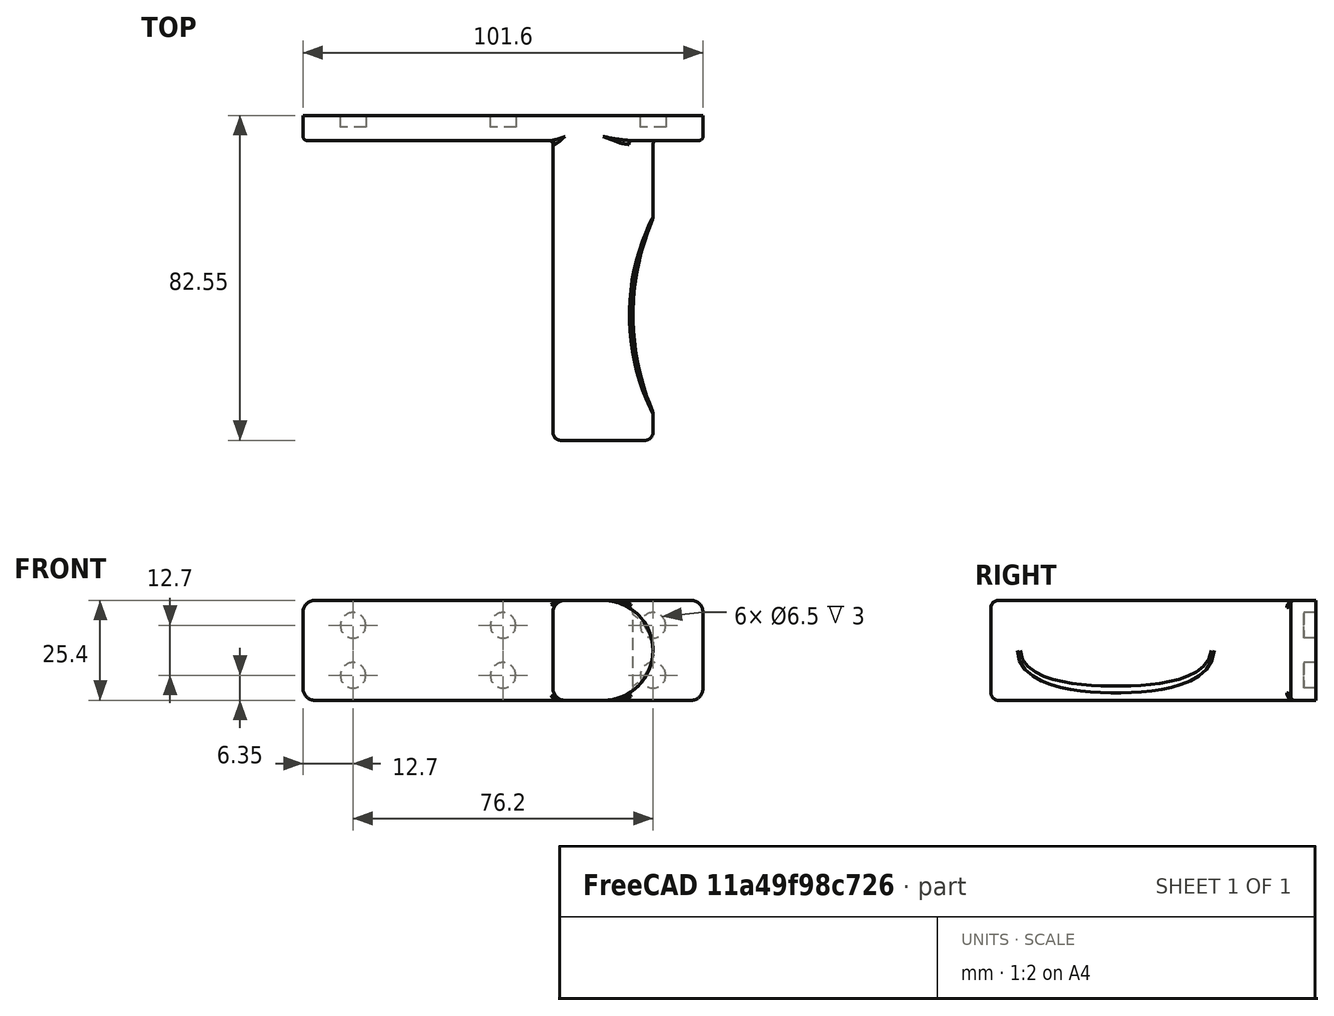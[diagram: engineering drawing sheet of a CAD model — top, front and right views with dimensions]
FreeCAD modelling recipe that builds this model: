
FCSTD DOCUMENT  (FreeCAD 0.19R)
Label: HeadphoneHolderFillets
License: All rights reserved
LicenseURL: http://en.wikipedia.org/wiki/All_rights_reserved
objects: Part::Cylinder×8, Part::Fillet×7, Part::Box×2, Part::MultiFuse×2, Part::Cut×1
note: 20 computed .brp shape members not serialized (recipe doc carries the construction recipe); baked Part::Feature solids carry a one-line shape summary decoded from their .brp

FEATURE [Part::Box] cube
  AttacherType = Attacher::AttachEngine3D
  Height = 25.4
  Length = 101.6
  Width = 6.35
FEATURE [Part::Cylinder] cylinder
  Angle = 360
  AttacherType = Attacher::AttachEngine3D
  Height = 76.2
  Placement = pos=(76.2,2.8e-15,12.7) rot=(1,0,0;1.5708rad)
  Radius = 12.7
FEATURE [Part::Box] cube001
  AttacherType = Attacher::AttachEngine3D
  Height = 25.4
  Length = 12.7
  Placement = pos=(76.2,0,0) rot=(0,0,1;3.14159rad)
  Width = 76.2
FEATURE [Part::MultiFuse] union
  Shapes = -> [cube,cylinder,cube001]
FEATURE [Part::Cylinder] cylinder001
  Angle = 360
  AttacherType = Attacher::AttachEngine3D
  Height = 3
  Placement = pos=(12.7,6.35,6.35) rot=(1,0,0;1.5708rad)
  Radius = 3.25
FEATURE [Part::Cylinder] cylinder002
  Angle = 360
  AttacherType = Attacher::AttachEngine3D
  Height = 3
  Placement = pos=(50.8,6.35,6.35) rot=(1,0,0;1.5708rad)
  Radius = 3.25
FEATURE [Part::Cylinder] cylinder003
  Angle = 360
  AttacherType = Attacher::AttachEngine3D
  Height = 3
  Placement = pos=(88.9,6.35,6.35) rot=(1,0,0;1.5708rad)
  Radius = 3.25
FEATURE [Part::Cylinder] cylinder004
  Angle = 360
  AttacherType = Attacher::AttachEngine3D
  Height = 3
  Placement = pos=(12.7,6.35,19.05) rot=(1,0,0;1.5708rad)
  Radius = 3.25
FEATURE [Part::Cylinder] cylinder005
  Angle = 360
  AttacherType = Attacher::AttachEngine3D
  Height = 3
  Placement = pos=(50.8,6.35,19.05) rot=(1,0,0;1.5708rad)
  Radius = 3.25
FEATURE [Part::Cylinder] cylinder006
  Angle = 360
  AttacherType = Attacher::AttachEngine3D
  Height = 3
  Placement = pos=(88.9,6.35,19.05) rot=(1,0,0;1.5708rad)
  Radius = 3.25
FEATURE [Part::Cylinder] cylinder007
  Angle = 360
  AttacherType = Attacher::AttachEngine3D
  Height = 50
  Placement = pos=(146.05,-44.45,0) rot=(0,0,1;0rad)
  Radius = 62.23
FEATURE [Part::MultiFuse] union001
  Shapes = -> [cylinder001,cylinder002,cylinder003,cylinder004,cylinder005,cylinder006,cylinder007]
FEATURE [Part::Cut] difference
  Base = -> union
  Tool = -> union001
FEATURE [Part::Fillet] Fillet
  Base = -> difference
  Edges = 6 edges r=3: [Edge2,Edge4,Edge10,Edge21,Edge26,Edge27]
FEATURE [Part::Fillet] Fillet001
  Base = -> Fillet
  Edges = 5 edges r=1: [Edge1,Edge5,Edge6,Edge7,Edge8]
FEATURE [Part::Fillet] Fillet002
  Base = -> Fillet001
  Edges = 5 edges r=1: [Edge29,Edge47,Edge49,Edge51,Edge53]
FEATURE [Part::Fillet] Fillet003
  Base = -> Fillet002
  Edges = 2 edges r=1: [Edge28,Edge50]
FEATURE [Part::Fillet] Fillet004
  Base = -> Fillet003
  Edges = 2 edges r=1: [Edge97,Edge98]
FEATURE [Part::Fillet] Fillet005
  Base = -> Fillet004
  Edges = 8 edges r=2: [Edge33,Edge54,Edge59,Edge75,Edge113,Edge117,Edge122,Edge130]
FEATURE [Part::Fillet] Fillet006
  Base = -> Fillet005
  Edges = 2 edges r=2: [Edge58,Edge108]
